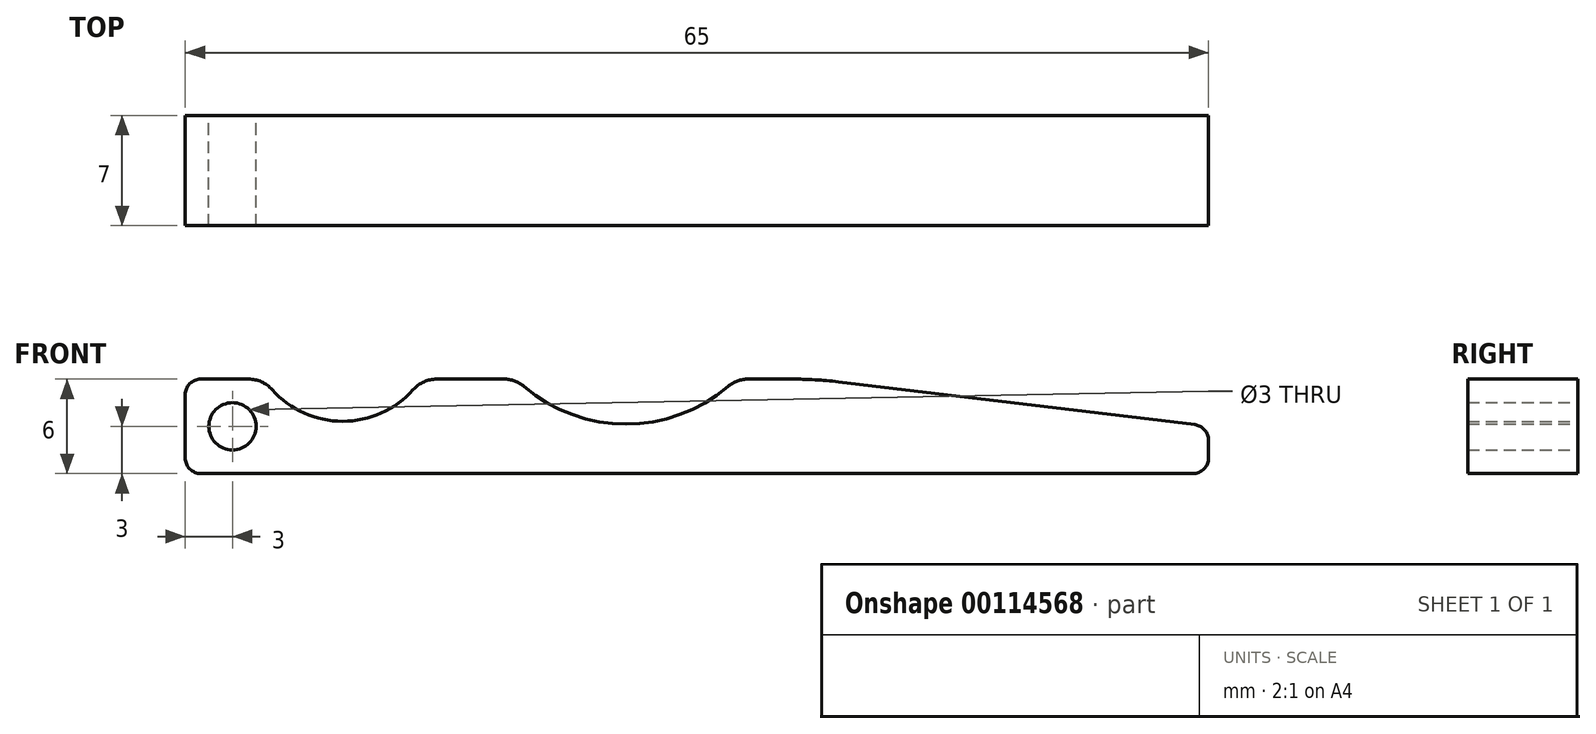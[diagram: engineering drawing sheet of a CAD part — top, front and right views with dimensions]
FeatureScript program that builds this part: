
annotation { "Feature Type Name" : "Feature", "Feature Type Description" : "" }
export const myFeature = defineFeature(function(context is Context, id is Id, definition is map)
    precondition{}
    {
        {
            var Q0;
            Q0=qCreatedBy(makeId("Front.planeOp"),FACE);
            var sketch = newSketch(context, id + "F0", { "sketchPlane" : qUnion([Q0])});
            skLineSegment(sketch, "E0", {"start": v(0, 0) * mm, "end": v(24, 0) * mm});
            skLineSegment(sketch, "E1", {"start": v(25, 1) * mm, "end": v(25, 2.11) * mm});
            skLineSegment(sketch, "E2", {"start": v(24.12, 3.1) * mm, "end": v(1.48, 5.82) * mm});
            skPoint(sketch, "E3.visualSharp", {"position": v(25, 3) * mm});
            skArc(sketch, "E3.filletArc", {"start": v(25, 2.11) * mm, "mid": v(24.75, 2.78) * mm, "end": v(24.12, 3.1) * mm});
            skPoint(sketch, "E4.visualSharp", {"position": v(25, 0) * mm});
            skArc(sketch, "E4.filletArc", {"start": v(24, 0) * mm, "mid": v(24.7, 0.3) * mm, "end": v(25, 1) * mm});
            skLineSegment(sketch, "E5", {"start": v(-35.98, 6) * mm, "end": v(-39, 6) * mm});
            skLineSegment(sketch, "E6", {"start": v(-40, 5) * mm, "end": v(-40, 1) * mm});
            skLineSegment(sketch, "E7", {"start": v(-39, 0) * mm, "end": v(0, 0) * mm});
            skCircle(sketch, "E8", {"center": v(-37, 3) * mm, "radius": 1.5 * mm});
            skLineSegment(sketch, "E9", {"start": v(-40, 3) * mm, "end": v(-27.58, 3) * mm, "construction": true});
            skPoint(sketch, "E10.visualSharp", {"position": v(-40, 6) * mm});
            skArc(sketch, "E10.filletArc", {"start": v(-39, 6) * mm, "mid": v(-39.7, 5.7) * mm, "end": v(-40, 5) * mm});
            skPoint(sketch, "E11.visualSharp", {"position": v(-40, 0) * mm});
            skArc(sketch, "E11.filletArc", {"start": v(-40, 1) * mm, "mid": v(-39.7, 0.3) * mm, "end": v(-39, 0) * mm});
            skPoint(sketch, "E12.visualSharp", {"position": v(0, 6) * mm});
            skArc(sketch, "E12.filletArc", {"start": v(1.48, 5.82) * mm, "mid": v(0, 5.96) * mm, "end": v(-1.5, 6) * mm});
            skArc(sketch, "E13", {"start": v(-34.48, 5.33) * mm, "mid": v(-30, 3.32) * mm, "end": v(-25.52, 5.33) * mm});
            skLineSegment(sketch, "E14", {"start": v(-29.97, 3.32) * mm, "end": v(-30, 9.32) * mm, "construction": true});
            skPoint(sketch, "E15.newPointB", {"position": v(-35, 6) * mm});
            skArc(sketch, "E15.filletArc", {"start": v(-34.48, 5.33) * mm, "mid": v(-35.16, 5.82) * mm, "end": v(-35.98, 6) * mm});
            skPoint(sketch, "E16.visualSharp", {"position": v(-25, 6) * mm});
            skArc(sketch, "E16.filletArc", {"start": v(-24.02, 6) * mm, "mid": v(-24.84, 5.82) * mm, "end": v(-25.52, 5.33) * mm});
            skLineSegment(sketch, "E17", {"start": v(-35.98, 6) * mm, "end": v(-24.02, 6) * mm, "construction": true});
            skArc(sketch, "E18", {"start": v(-18.48, 5.52) * mm, "mid": v(-12, 3.14) * mm, "end": v(-5.52, 5.52) * mm});
            skLineSegment(sketch, "E19", {"start": v(-12, 13.14) * mm, "end": v(-12, 3.14) * mm, "construction": true});
            skLineSegment(sketch, "E20", {"start": v(-24.02, 6) * mm, "end": v(-19.77, 6) * mm});
            skLineSegment(sketch, "E21", {"start": v(-4.23, 6) * mm, "end": v(-1.5, 6) * mm});
            skPoint(sketch, "E22.visualSharp", {"position": v(-19, 6) * mm});
            skArc(sketch, "E22.filletArc", {"start": v(-18.48, 5.52) * mm, "mid": v(-19.08, 5.88) * mm, "end": v(-19.77, 6) * mm});
            skPoint(sketch, "E23.visualSharp", {"position": v(-5, 6) * mm});
            skArc(sketch, "E23.filletArc", {"start": v(-4.23, 6) * mm, "mid": v(-4.92, 5.88) * mm, "end": v(-5.52, 5.52) * mm});
            skSolve(sketch);
        }
        {
            var Q0;
            Q0=makeQuery(id+"F0.imprint","IMPRINT",FACE,{"disambiguationData":[TD([[makeQuery(id+"F0.imprint","IMPRINT",EDGE,{"derivedFrom":sQuery(id+"F0.wireOp",EDGE,"E0")}),1.0]])]});
            extrude(context, id + "F1", {"entities" : qUnion([Q0]), "depth" : 7 * mm});
        }
    });
